# Revit family: LM
name_source: partatom
category: Lighting Fixtures
units: mm (PartAtom-declared; Revit-internal decimal feet)

## family parameters
Cut with Voids When Loaded = No
Host = Face
Light Source = No
OmniClass Number = 23.80.70.11.21
OmniClass Title = Emergency Lighting
Part Type = Normal
Room Calculation Point = No
Round Connector Dimension = Use Diameter
Shared = No

## types (2) — shared parameters
120 Voltage = Yes
277 Voltage = No
Apparent Load = 3 VA
Default Elevation = 48.000"
Depth = 3.875"
Description = Emergency Light, Steel Housing
Finish = White
Height = 5.750"
Lamp = LED Lamp
Lens = Glass
Load Classification = Lighting
Manufacturer = Dual-Lite Lighting
Model = LM
Power factor = 1
URL = https://www.currentlighting.com
Voltage = 120 V
Watt = 130 W
Wattage Comments = 130W
Width = 13.500"

## per-type parameters (varying)
| type | Housing | LAMP Height |
| LM 1 | LM Housing : LM Housing1 | 4.000" |
| LM 2 | LM Housing : LM Housing 2 | 2.000" |

## geometry (parser evidence)
native form markers: Sweep x8
no freeform markers — native parametric forms only
